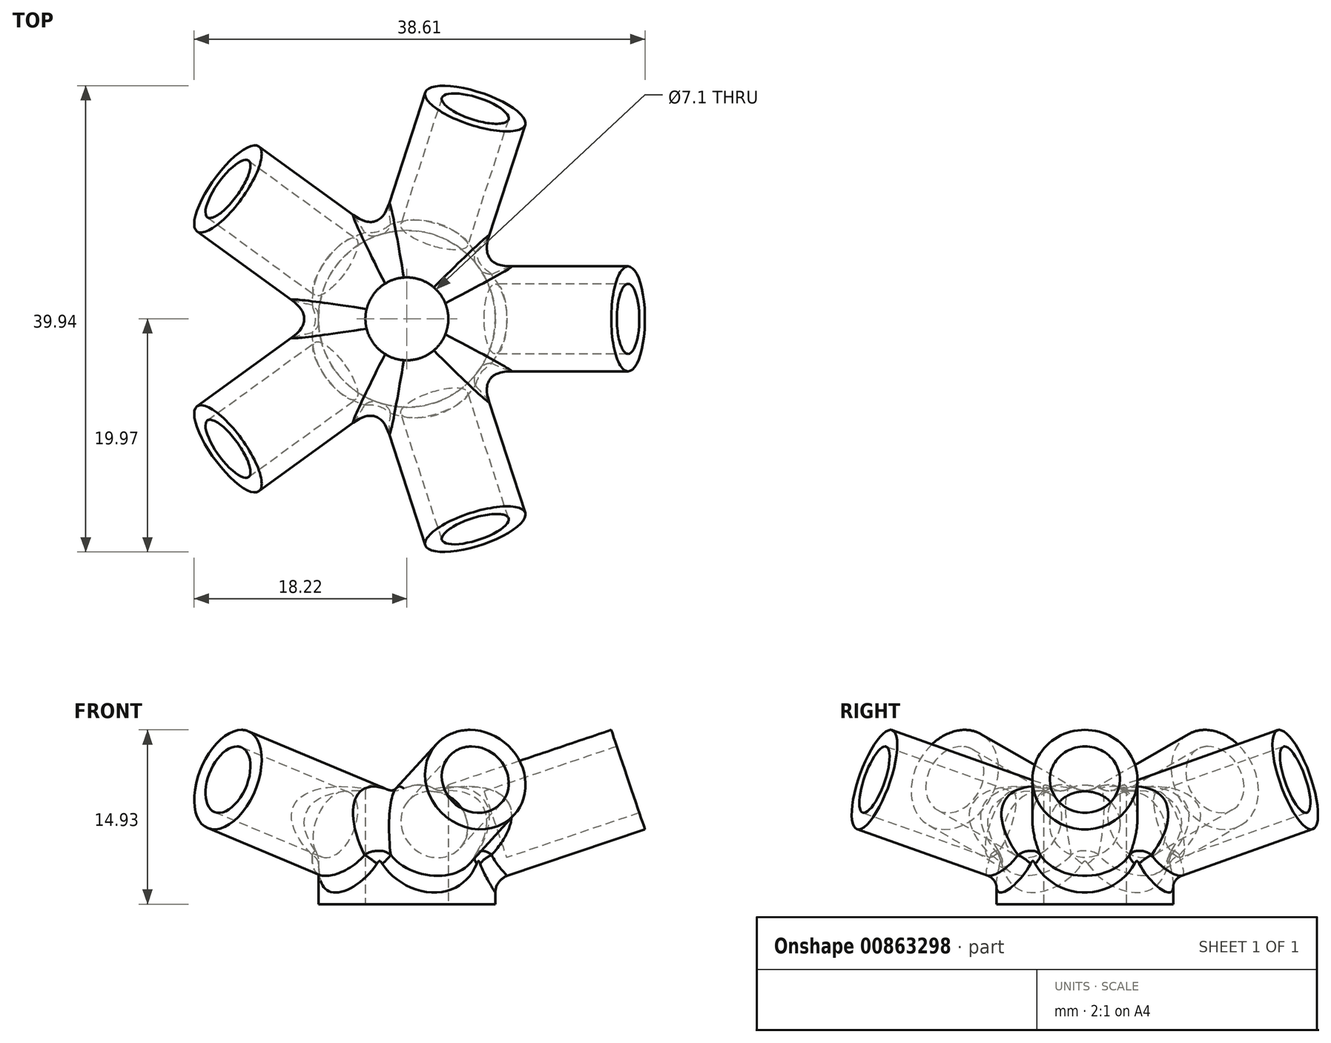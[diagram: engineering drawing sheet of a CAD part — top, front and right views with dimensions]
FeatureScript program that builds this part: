
annotation { "Feature Type Name" : "Feature", "Feature Type Description" : "" }
export const myFeature = defineFeature(function(context is Context, id is Id, definition is map)
    precondition{}
    {
        {
            var Q0;
            Q0=qCreatedBy(makeId("Front.planeOp"),FACE);
            var sketch = newSketch(context, id + "F0", { "sketchPlane" : qUnion([Q0])});
            skLineSegment(sketch, "E0", {"start": v(0, 0) * mm, "end": v(18.95, 6.4) * mm, "construction": true});
            skLineSegment(sketch, "E1", {"start": v(0, 0) * mm, "end": v(1.44, -4.26) * mm});
            skLineSegment(sketch, "E2", {"start": v(18.95, 6.4) * mm, "end": v(20.39, 2.15) * mm});
            skLineSegment(sketch, "E3", {"start": v(1.44, -4.26) * mm, "end": v(20.39, 2.15) * mm});
            skLineSegment(sketch, "E4", {"start": v(19.9, 3.57) * mm, "end": v(8.54, -0.28) * mm});
            skLineSegment(sketch, "E5", {"start": v(8.54, -0.28) * mm, "end": v(7.58, 2.56) * mm});
            skLineSegment(sketch, "E6", {"start": v(7.58, 2.56) * mm, "end": v(0, 0) * mm});
            skLineSegment(sketch, "E7", {"start": v(0, 0) * mm, "end": v(0, 41.35) * mm, "construction": true});
            skLineSegment(sketch, "E8", {"start": v(1.44, -4.26) * mm, "end": v(0, -4.26) * mm, "construction": true});
            skLineSegment(sketch, "E9", {"start": v(7.58, 2.56) * mm, "end": v(7.58, -4.26) * mm, "construction": true});
            skLineSegment(sketch, "E10", {"start": v(7.58, -4.26) * mm, "end": v(1.44, -4.26) * mm, "construction": true});
            skLineSegment(sketch, "E11", {"start": v(0, -4.26) * mm, "end": v(7.58, -4.26) * mm});
            skLineSegment(sketch, "E12", {"start": v(7.58, -4.26) * mm, "end": v(7.58, 2.56) * mm});
            skLineSegment(sketch, "E13", {"start": v(0, 2.56) * mm, "end": v(7.58, 2.56) * mm});
            skLineSegment(sketch, "E14", {"start": v(0, 2.56) * mm, "end": v(0, -4.26) * mm});
            skSolve(sketch);
        }
        {
            var Q0;
            {var subQ1=sQuery(id+"F0.wireOp",EDGE,"E4");Q0=makeQuery(id+"F0.imprint","IMPRINT",FACE,{"disambiguationData":[TD([[makeQuery(id+"F0.imprint","IMPRINT",EDGE,{"derivedFrom":subQ1}),1.0]])]});}
            var Q1;
            {var subQ0=sQuery(id+"F0.wireOp",EDGE,"E1");Q1=makeQuery(id+"F0.imprint","IMPRINT",FACE,{"disambiguationData":[TD([[makeQuery(id+"F0.imprint","IMPRINT",EDGE,{"derivedFrom":subQ0}),1.0]])]});}
            var Q2;
            Q2=sQuery(id+"F0.wireOp",EDGE,"E0");
            revolve(context, id + "F1", {"surfaceOperationType" : NewSurfaceOperationType.NEW, "entities" : qUnion([Q0, Q1]), "axis" : qUnion([Q2]), "revolveType" : RevolveType.FULL});
        }
        {
            var Q0;
            Q0=makeQuery(id+"F1.opRevolve","SWEPT_BODY",BODY,{"disambiguationData":[OSD([sQuery(id+"F0.wireOp",EDGE,"E1"),sQuery(id+"F0.wireOp",EDGE,"E2"),sQuery(id+"F0.wireOp",EDGE,"E3"),sQuery(id+"F0.wireOp",EDGE,"E4"),sQuery(id+"F0.wireOp",EDGE,"E5"),sQuery(id+"F0.wireOp",EDGE,"E6")])]});
            var Q1;
            Q1=sQuery(id+"F0.wireOp",EDGE,"E7");
            circularPattern(context, id + "F2", {"operationType" : NewBodyOperationType.ADD, "entities" : qUnion([Q0]), "axis" : qUnion([Q1]), "angle" : 360 * degree, "instanceCount" : 5, "equalSpace" : true});
        }
        {
            var Q0;
            {var subQ0=sQuery(id+"F0.wireOp",EDGE,"E1");Q0=makeQuery(id+"F0.imprint","IMPRINT",FACE,{"disambiguationData":[TD([[makeQuery(id+"F0.imprint","IMPRINT",EDGE,{"derivedFrom":subQ0}),-1.0]])]});}
            var Q1;
            {var subQ0=sQuery(id+"F0.wireOp",EDGE,"E1");Q1=makeQuery(id+"F0.imprint","IMPRINT",FACE,{"disambiguationData":[TD([[makeQuery(id+"F0.imprint","IMPRINT",EDGE,{"derivedFrom":subQ0}),1.0]])]});}
            var Q2;
            {var subQ0=sQuery(id+"F0.wireOp",EDGE,"E11");var subQ3=sQuery(id+"F0.wireOp",EDGE,"E12");var subQ5=makeQuery(id+"F0.imprint","INTERSECT",VERTEX,{"derivedFrom":[subQ0,subQ3]});Q2=makeQuery(id+"F0.imprint","IMPRINT",FACE,{"disambiguationData":[TD([[makeQuery(id+"F0.imprint","IMPRINT",EDGE,{"disambiguationData":[TD([[subQ5,-1.0]])],"derivedFrom":subQ3}),1.0]])]});}
            var Q3;
            {var subQ0=sQuery(id+"F0.wireOp",EDGE,"E6");Q3=makeQuery(id+"F0.imprint","IMPRINT",FACE,{"disambiguationData":[TD([[makeQuery(id+"F0.imprint","IMPRINT",EDGE,{"derivedFrom":subQ0}),-1.0]])]});}
            var Q4;
            Q4=sQuery(id+"F0.wireOp",EDGE,"E13");
            var Q5;
            Q5=sQuery(id+"F0.wireOp",EDGE,"E14");
            var Q6;
            Q6=sQuery(id+"F0.wireOp",EDGE,"E7");
            revolve(context, id + "F3", {"surfaceOperationType" : NewSurfaceOperationType.NEW, "entities" : qUnion([Q0, Q1, Q2, Q3]), "surfaceEntities" : qUnion([Q4, Q5]), "axis" : qUnion([Q6]), "revolveType" : RevolveType.FULL});
        }
        {
            var Q0;
            Q0=makeQuery(id+"F3.opRevolve","SWEPT_FACE",FACE,{"disambiguationData":[OSD([sQuery(id+"F0.wireOp",EDGE,"E11")])]});
            var sketch = newSketch(context, id + "F4", { "sketchPlane" : qUnion([Q0])});
            skCircle(sketch, "E15", {"center": v(0, 0) * mm, "radius": 3.55 * mm});
            skSolve(sketch);
        }
        {
            var Q0;
            Q0=makeQuery(id+"F4.imprint","IMPRINT",FACE,{"disambiguationData":[TD([[makeQuery(id+"F4.imprint","IMPRINT",EDGE,{"derivedFrom":sQuery(id+"F4.wireOp",EDGE,"E15")}),1.0]])]});
            extrude(context, id + "F5", {"entities" : qUnion([Q0]), "operationType" : NewBodyOperationType.REMOVE, "endBound" : BoundingType.THROUGH_ALL, "oppositeDirection" : true, "depth" : 25 * mm, "offsetDistance" : 25 * mm});
        }
        {
            var Q0;
            Q0=makeQuery(id+"F1.opRevolve","SWEPT_BODY",BODY,{"disambiguationData":[OSD([sQuery(id+"F0.wireOp",EDGE,"E1"),sQuery(id+"F0.wireOp",EDGE,"E2"),sQuery(id+"F0.wireOp",EDGE,"E3"),sQuery(id+"F0.wireOp",EDGE,"E4"),sQuery(id+"F0.wireOp",EDGE,"E5"),sQuery(id+"F0.wireOp",EDGE,"E6")])]});
            var Q1;
            Q1=makeQuery(id+"F3.opRevolve","SWEPT_BODY",BODY,{"disambiguationData":[OSD([sQuery(id+"F0.wireOp",EDGE,"E11"),sQuery(id+"F0.wireOp",EDGE,"E12"),sQuery(id+"F0.wireOp",EDGE,"E13"),sQuery(id+"F0.wireOp",EDGE,"E14")])]});
            booleanBodies(context, id + "F6", {"operationType" : BooleanOperationType.UNION, "tools" : qUnion([Q0, Q1])});
        }
        {
            var Q0;
            {var subQ0=makeQuery(id+"F1.opRevolve","SWEPT_FACE",FACE,{"disambiguationData":[OSD([sQuery(id+"F0.wireOp",EDGE,"E3")])]});Q0=makeQuery(id+"F2.boolean.opBoolean","INTERSECT",EDGE,{"derivedFrom":[makeQuery(id+"F2.opPattern","COPY",FACE,{"derivedFrom":subQ0,"instanceName":"2"}),makeQuery(id+"F2.opPattern","COPY",FACE,{"derivedFrom":subQ0,"instanceName":"3"})]});}
            var Q1;
            {var subQ0=makeQuery(id+"F1.opRevolve","SWEPT_FACE",FACE,{"disambiguationData":[OSD([sQuery(id+"F0.wireOp",EDGE,"E3")])]});Q1=makeQuery(id+"F2.boolean.opBoolean","INTERSECT",EDGE,{"derivedFrom":[makeQuery(id+"F2.opPattern","COPY",FACE,{"derivedFrom":subQ0,"instanceName":"1"}),makeQuery(id+"F2.opPattern","COPY",FACE,{"derivedFrom":subQ0,"instanceName":"2"})]});}
            var Q2;
            {var subQ0=makeQuery(id+"F1.opRevolve","SWEPT_FACE",FACE,{"disambiguationData":[OSD([sQuery(id+"F0.wireOp",EDGE,"E3")])]});Q2=makeQuery(id+"F2.boolean.opBoolean","INTERSECT",EDGE,{"derivedFrom":[subQ0,makeQuery(id+"F2.opPattern","COPY",FACE,{"derivedFrom":subQ0,"instanceName":"1"})]});}
            var Q3;
            {var subQ0=makeQuery(id+"F1.opRevolve","SWEPT_FACE",FACE,{"disambiguationData":[OSD([sQuery(id+"F0.wireOp",EDGE,"E3")])]});Q3=makeQuery(id+"F2.boolean.opBoolean","INTERSECT",EDGE,{"derivedFrom":[subQ0,makeQuery(id+"F2.opPattern","COPY",FACE,{"derivedFrom":subQ0,"instanceName":"4"})]});}
            var Q4;
            {var subQ0=makeQuery(id+"F1.opRevolve","SWEPT_FACE",FACE,{"disambiguationData":[OSD([sQuery(id+"F0.wireOp",EDGE,"E3")])]});Q4=makeQuery(id+"F2.boolean.opBoolean","INTERSECT",EDGE,{"derivedFrom":[makeQuery(id+"F2.opPattern","COPY",FACE,{"derivedFrom":subQ0,"instanceName":"3"}),makeQuery(id+"F2.opPattern","COPY",FACE,{"derivedFrom":subQ0,"instanceName":"4"})]});}
            fillet(context, id + "F7", {"entities" : qUnion([Q0, Q1, Q2, Q3, Q4]), "radius" : 2 * mm, "tangentPropagation" : true, "rho" : 0.5, "crossSection" : FilletCrossSection.CONIC, "allowEdgeOverflow" : false});
        }
        {
            var Q0;
            Q0=makeQuery(id+"F6.opBoolean","INTERSECT",EDGE,{"derivedFrom":[makeQuery(id+"F3.opRevolve","SWEPT_FACE",FACE,{"disambiguationData":[OSD([sQuery(id+"F0.wireOp",EDGE,"E12")])]}),makeQuery(id+"F1.opRevolve","SWEPT_FACE",FACE,{"disambiguationData":[OSD([sQuery(id+"F0.wireOp",EDGE,"E3")])]})]});
            var Q1;
            Q1=makeQuery(id+"F6.opBoolean","INTERSECT",EDGE,{"derivedFrom":[makeQuery(id+"F3.opRevolve","SWEPT_FACE",FACE,{"disambiguationData":[OSD([sQuery(id+"F0.wireOp",EDGE,"E12")])]}),makeQuery(id+"F2.opPattern","COPY",FACE,{"derivedFrom":makeQuery(id+"F1.opRevolve","SWEPT_FACE",FACE,{"disambiguationData":[OSD([sQuery(id+"F0.wireOp",EDGE,"E3")])]}),"instanceName":"4"})]});
            var Q2;
            Q2=makeQuery(id+"F6.opBoolean","INTERSECT",EDGE,{"derivedFrom":[makeQuery(id+"F3.opRevolve","SWEPT_FACE",FACE,{"disambiguationData":[OSD([sQuery(id+"F0.wireOp",EDGE,"E12")])]}),makeQuery(id+"F2.opPattern","COPY",FACE,{"derivedFrom":makeQuery(id+"F1.opRevolve","SWEPT_FACE",FACE,{"disambiguationData":[OSD([sQuery(id+"F0.wireOp",EDGE,"E3")])]}),"instanceName":"1"})]});
            var Q3;
            Q3=makeQuery(id+"F6.opBoolean","INTERSECT",EDGE,{"derivedFrom":[makeQuery(id+"F3.opRevolve","SWEPT_FACE",FACE,{"disambiguationData":[OSD([sQuery(id+"F0.wireOp",EDGE,"E12")])]}),makeQuery(id+"F2.opPattern","COPY",FACE,{"derivedFrom":makeQuery(id+"F1.opRevolve","SWEPT_FACE",FACE,{"disambiguationData":[OSD([sQuery(id+"F0.wireOp",EDGE,"E3")])]}),"instanceName":"2"})]});
            var Q4;
            Q4=makeQuery(id+"F6.opBoolean","INTERSECT",EDGE,{"derivedFrom":[makeQuery(id+"F3.opRevolve","SWEPT_FACE",FACE,{"disambiguationData":[OSD([sQuery(id+"F0.wireOp",EDGE,"E12")])]}),makeQuery(id+"F2.opPattern","COPY",FACE,{"derivedFrom":makeQuery(id+"F1.opRevolve","SWEPT_FACE",FACE,{"disambiguationData":[OSD([sQuery(id+"F0.wireOp",EDGE,"E3")])]}),"instanceName":"3"})]});
            fillet(context, id + "F8", {"entities" : qUnion([Q0, Q1, Q2, Q3, Q4]), "radius" : 1.5 * mm, "allowEdgeOverflow" : false});
        }
    });
